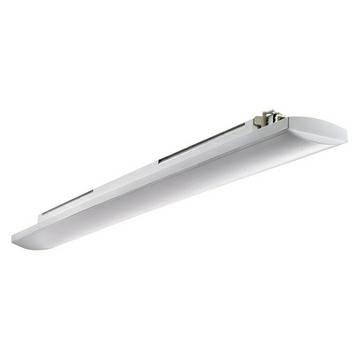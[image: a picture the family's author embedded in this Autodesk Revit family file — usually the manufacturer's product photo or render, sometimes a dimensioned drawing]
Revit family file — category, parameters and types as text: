
# Revit family: Lighting-Industrial-GEWISS-SMART[3]PLUS-WATERTIGHT-LED-EMERGENCY_OPAL_1600mm
name_source: partatom
category: Apparecchi per illuminazione
units: mm (PartAtom-declared; Revit-internal decimal feet)

## family parameters
Condiviso = No
Host = Superficie
Numero OmniClass = 23.80.70.11
Punto di calcolo locali = No
Quota connettore circolare = Usa diametro
Sorgente d'illuminazione = No
Taglio con vuoti quando caricato = No
Tipo di parte = Normale
Titolo OmniClass = Luminaries for Internal Lighting

## types (1)
- Lighting-Industrial-GEWISS-SMART[3]PLUS-WATERTIGHT-LED-EMERGENCY_OPAL_1600mm
    Application = Indoor
    Carico apparente = 55 VA
    Catalogue = LIGHTING
    Catalogue Range = SMART[3] PLUS
    Colour temperature = 5700 K (CRI > 90)
    Colour temperature: = 5700 K (CRI > 90)
    Commenti sul wattaggio = 55W
    Descrizione = SMART3 PLUS 1600 EMERG DT1+DT6 HE OPAL 9 57
    Efficiency class of integrated LEDs = A ÷ A++
    Electrocod = 2434
    Ganci = GEWISS  - ALLUMINIO
    Glow Wire Test = 850°C
    IDF = 7a91b3af-7b8f-4b45-9b1e-8da76f6e3765
    IDT = fc3a2e1b-6a5f-4da6-a0ae-96bfc5d9bbbb
    IP degree = IP66/IP69
    Immagine tipo = GWS3158P.jpg
    Insulation class = II
    Lamp = LED
    Lampada = LED
    Length = 1600 mm
    Lumen output (lm) = 5200
    Lunghezza Lampada = 1600 mm  [stored 5.24934 ft]
    Modello = GWS3325AP957
    Operating temperature: = ND
    Produttore = GEWISS S.p.A.
    Prospetto di default = 1219 mm
    SEO = Ceiling
    Schermo. = Gewiss - Led Acceso
    Shield type = Opal
    Shock resistance = IK08
    Stampa 1_100 = Sì
    Stampa 1_200 = No
    Struttura = GEWISS - SMART 3 - GRIGIO
    System power = 50 W
    Technical sheet = https://www.gewiss.com
    Type of light source = LED - Not replaceable
    URL = https://www.gewiss.com
    Version file RFA = 20.0
    Voltage = 220-240 V
    Warranty = ND
    Working temperature = ND

note: [stored X ft] marks values corroborated as IEEE doubles in the binary element streams (Revit-internal decimal feet)
